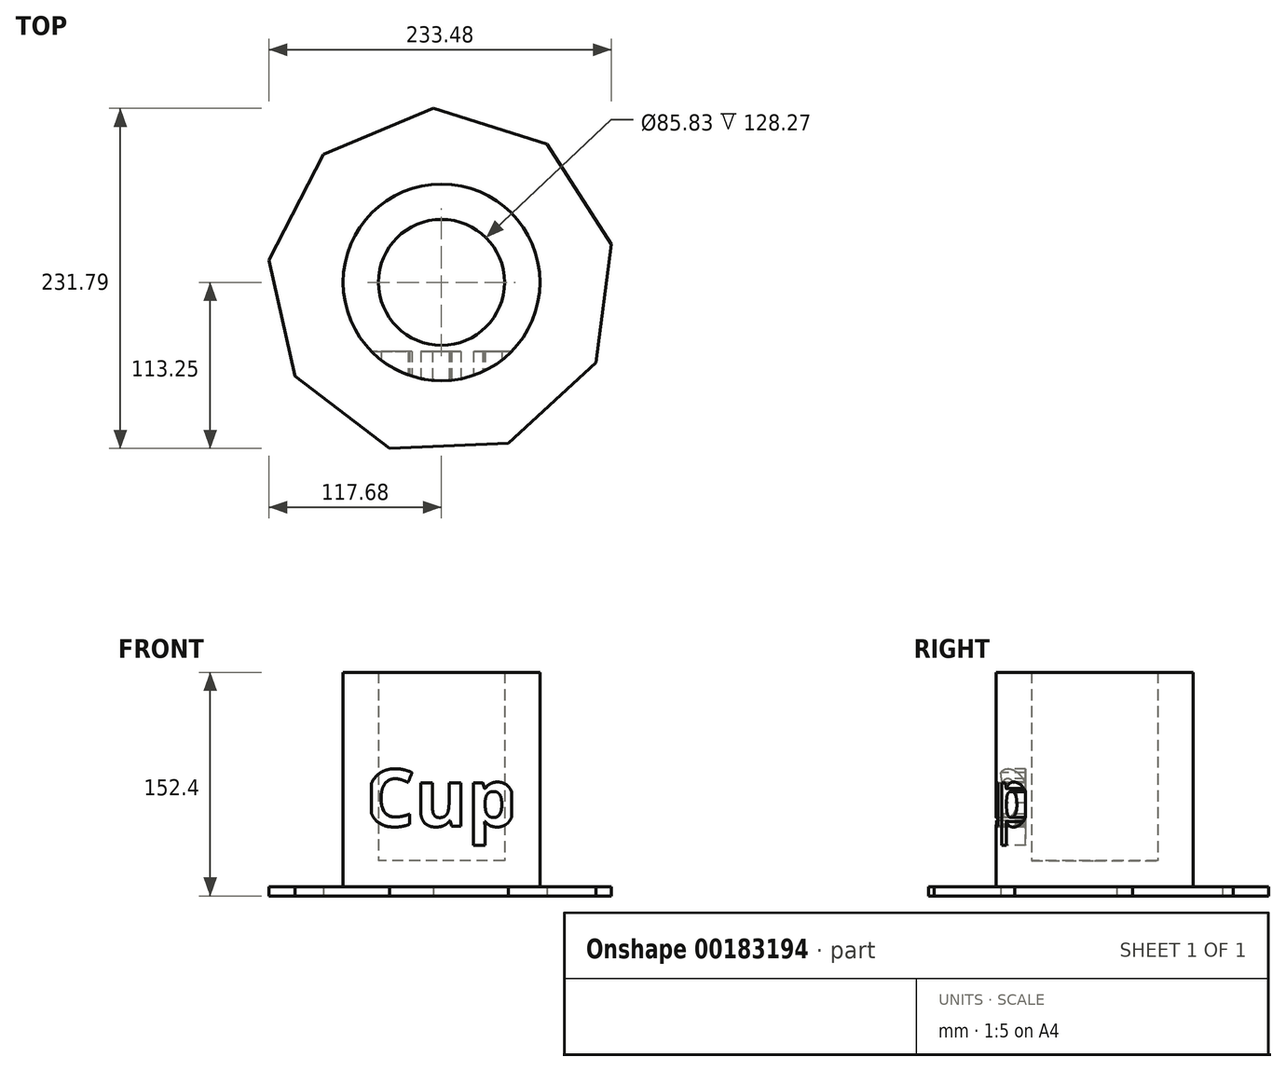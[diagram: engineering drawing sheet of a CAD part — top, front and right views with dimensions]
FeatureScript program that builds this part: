
annotation { "Feature Type Name" : "Feature", "Feature Type Description" : "" }
export const myFeature = defineFeature(function(context is Context, id is Id, definition is map)
    precondition{}
    {
        {
            var Q0;
            Q0=qCreatedBy(makeId("Top.planeOp"),FACE);
            var sketch = newSketch(context, id + "F0", { "sketchPlane" : qUnion([Q0])});
            skCircle(sketch, "E0", {"center": v(0, 0) * mm, "radius": 67.05 * mm});
            skSolve(sketch);
        }
        {
            var Q0;
            Q0=makeQuery(id+"F0.imprint","IMPRINT",FACE,{"disambiguationData":[TD([[makeQuery(id+"F0.imprint","IMPRINT",EDGE,{"derivedFrom":sQuery(id+"F0.wireOp",EDGE,"E0")}),1.0]])]});
            var Q1;
            Q1 = qSketchRegion(id + "F4", true);
            extrude(context, id + "F1", {"entities" : qUnion([Q0, Q1]), "depth" : 152.4 * mm});
        }
        {
            var Q0;
            Q0=makeQuery(id+"F1.opExtrude","CAP_FACE",FACE,{"disambiguationData":[OSD([sQuery(id+"F0.wireOp",EDGE,"E0")])],"isStart":false});
            shell(context, id + "F2", {"entities" : qUnion([Q0]), "thickness" : 24.13 * mm});
        }
        {
            var Q0;
            Q0=qCreatedBy(makeId("Front.planeOp"),FACE);
            cPlane(context, id + "F3", {"entities" : qUnion([Q0]), "cplaneType" : CPlaneType.OFFSET, "offset" : 68.58 * mm, "width" : 152.4 * mm, "height" : 152.4 * mm});
        }
        {
            var Q0;
            Q0=qCreatedBy(id+"F3.planeOp",FACE);
            var sketch = newSketch(context, id + "F4", { "sketchPlane" : qUnion([Q0])});
            skText(sketch, "E1", { "text": "Cup", "fontName": "OpenSans-Bold.ttf"});
            const initialGuessF4  = {"E1": [-0.05278, 0.04747, 1, 0, 0.03905]};
            skSetInitialGuess(sketch, initialGuessF4);
            skSolve(sketch);
        }
        {
            var Q0;
            Q0 = qSketchRegion(id + "F4", true);
            extrude(context, id + "F5", {"entities" : qUnion([Q0]), "operationType" : NewBodyOperationType.REMOVE, "oppositeDirection" : true, "depth" : 21.59 * mm});
        }
        {
            var Q0;
            Q0=qCreatedBy(makeId("Top.planeOp"),FACE);
            var sketch = newSketch(context, id + "F6", { "sketchPlane" : qUnion([Q0])});
            skCircle(sketch, "E2.cCircle", {"center": v(0, 0) * mm, "radius": 111.5 * mm, "construction": true});
            skLineSegment(sketch, "E2.0", {"start": v(105.37, -54.57) * mm, "end": v(45.65, -109.54) * mm});
            skLineSegment(sketch, "E2.1", {"start": v(45.65, -109.54) * mm, "end": v(-35.44, -113.25) * mm});
            skLineSegment(sketch, "E2.2", {"start": v(-35.44, -113.25) * mm, "end": v(-99.94, -63.97) * mm});
            skLineSegment(sketch, "E2.3", {"start": v(-99.94, -63.97) * mm, "end": v(-117.68, 15.24) * mm});
            skLineSegment(sketch, "E2.4", {"start": v(-117.68, 15.24) * mm, "end": v(-80.36, 87.32) * mm});
            skLineSegment(sketch, "E2.5", {"start": v(-80.36, 87.32) * mm, "end": v(-5.43, 118.54) * mm});
            skLineSegment(sketch, "E2.6", {"start": v(-5.43, 118.54) * mm, "end": v(72.04, 94.3) * mm});
            skLineSegment(sketch, "E2.7", {"start": v(72.04, 94.3) * mm, "end": v(115.8, 25.93) * mm});
            skLineSegment(sketch, "E2.8", {"start": v(115.8, 25.93) * mm, "end": v(105.37, -54.57) * mm});
            skPoint(sketch, "E2.0.midPoint", {"position": v(75.5, -82.05) * mm});
            skSolve(sketch);
        }
        {
            var Q0;
            Q0=makeQuery(id+"F6.imprint","IMPRINT",FACE,{"disambiguationData":[TD([[makeQuery(id+"F6.imprint","IMPRINT",EDGE,{"derivedFrom":sQuery(id+"F6.wireOp",EDGE,"E2.0")}),-1.0]])]});
            extrude(context, id + "F7", {"entities" : qUnion([Q0]), "operationType" : NewBodyOperationType.ADD, "depth" : 6.35 * mm});
        }
    });
